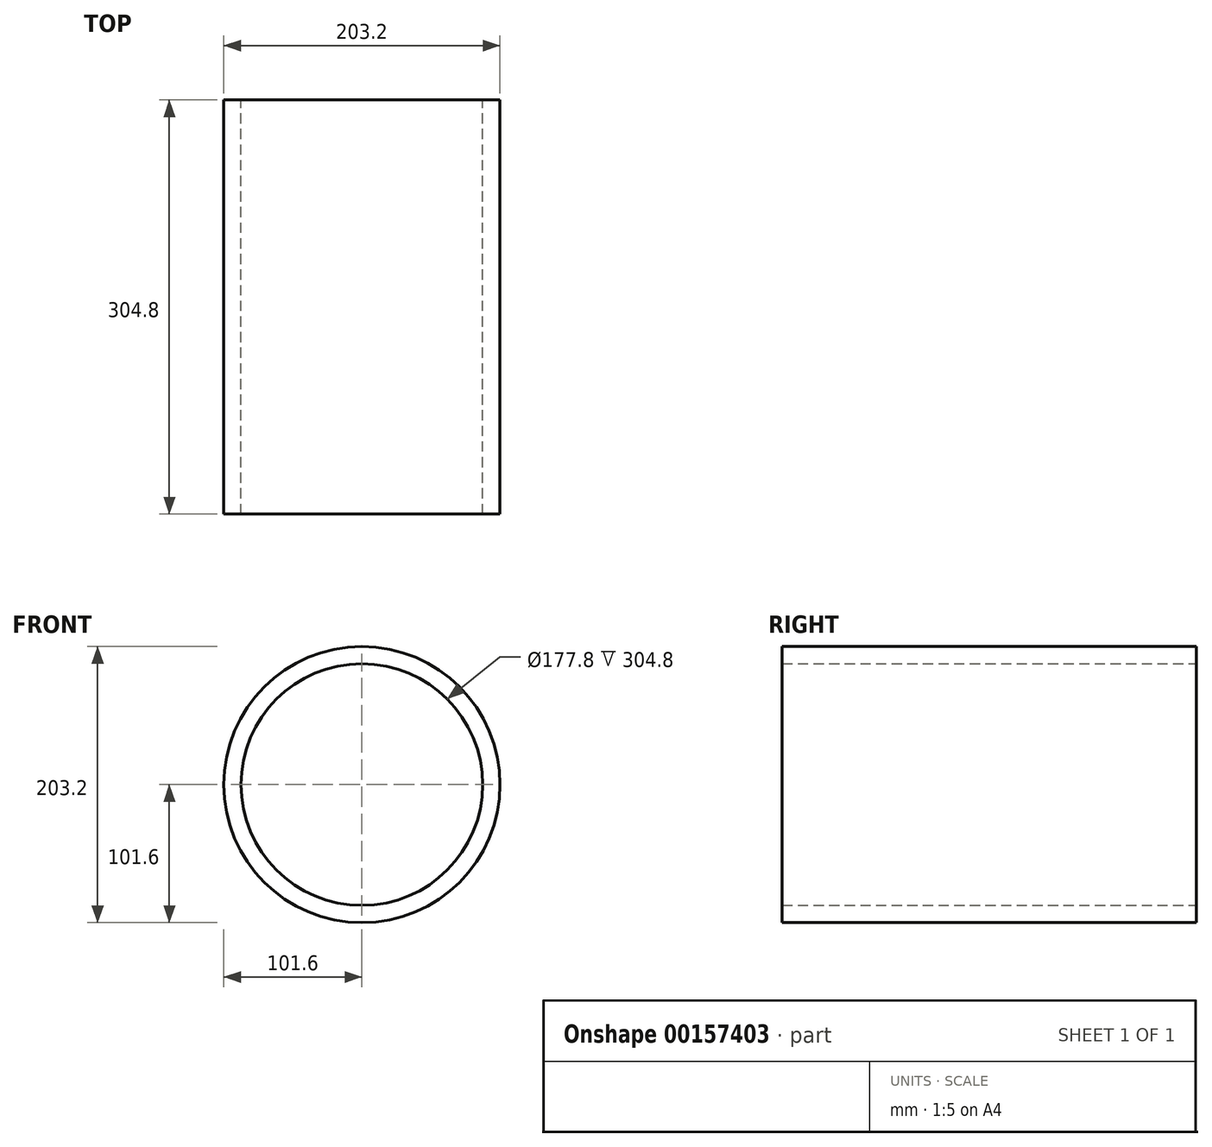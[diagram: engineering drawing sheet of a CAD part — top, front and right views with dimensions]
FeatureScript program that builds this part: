
annotation { "Feature Type Name" : "Feature", "Feature Type Description" : "" }
export const myFeature = defineFeature(function(context is Context, id is Id, definition is map)
    precondition{}
    {
        {
            var Q0;
            Q0=qCreatedBy(makeId("Front.planeOp"),FACE);
            var sketch = newSketch(context, id + "F0", { "sketchPlane" : qUnion([Q0])});
            skCircle(sketch, "E0", {"center": v(0, 0) * mm, "radius": 101.6 * mm});
            skCircle(sketch, "E1", {"center": v(0, 0) * mm, "radius": 88.9 * mm});
            skSolve(sketch);
        }
        {
            var Q0;
            Q0 = qSketchRegion(id + "F0", true);
            extrude(context, id + "F1", {"entities" : qUnion([Q0]), "depth" : 304.8 * mm});
        }
    });
